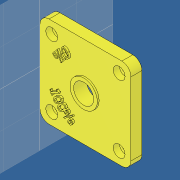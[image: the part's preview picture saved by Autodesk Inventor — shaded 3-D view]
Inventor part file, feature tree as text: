
AUTODESK INVENTOR PART (.ipt)
format: ipt  version: 2019 (Build 230136000, 136)  size: 387,072 bytes
history: native  units: mm
features: extrude x2, sketch x1, other x1, hole x1
ambient origin geometry x8: Origin, YZ Plane, XZ Plane, XY Plane, X Axis, Y Axis, Z Axis, Center Point
bodies: Volumenkörper1 (feature_tree)
feature tree (5):
  sketch  "Skizze1"  dims[d0=50.0mm d1=50.0mm d2=5.0mm d3=37.0mm d4=11.0mm d5=30.0mm d6=15.0mm d7=6.0mm d8=0.0mm d9=1.0mm d10=0.0mm d11=1.0mm d12=0.0mm d13=3.4mm d14=6.0mm d15=6.5mm d16=3.4mm d17=90.0deg d18=8.0mm d19=20.594885mm]
  extrude  "Extrusion1"  Depth=6.0mm TaperAngle=0.0deg
  extrude  "Extrusion2"  Depth=3.4mm TaperAngle=0.0deg
  other  "Prägen1"
  hole  "Bohrung1"  [1 undecoded]
note: 1 required parameter value undecoded (feature->parameter linkage not recoverable at this tier; creation-order binding heuristic only, values carry confidence <= 0.55)
